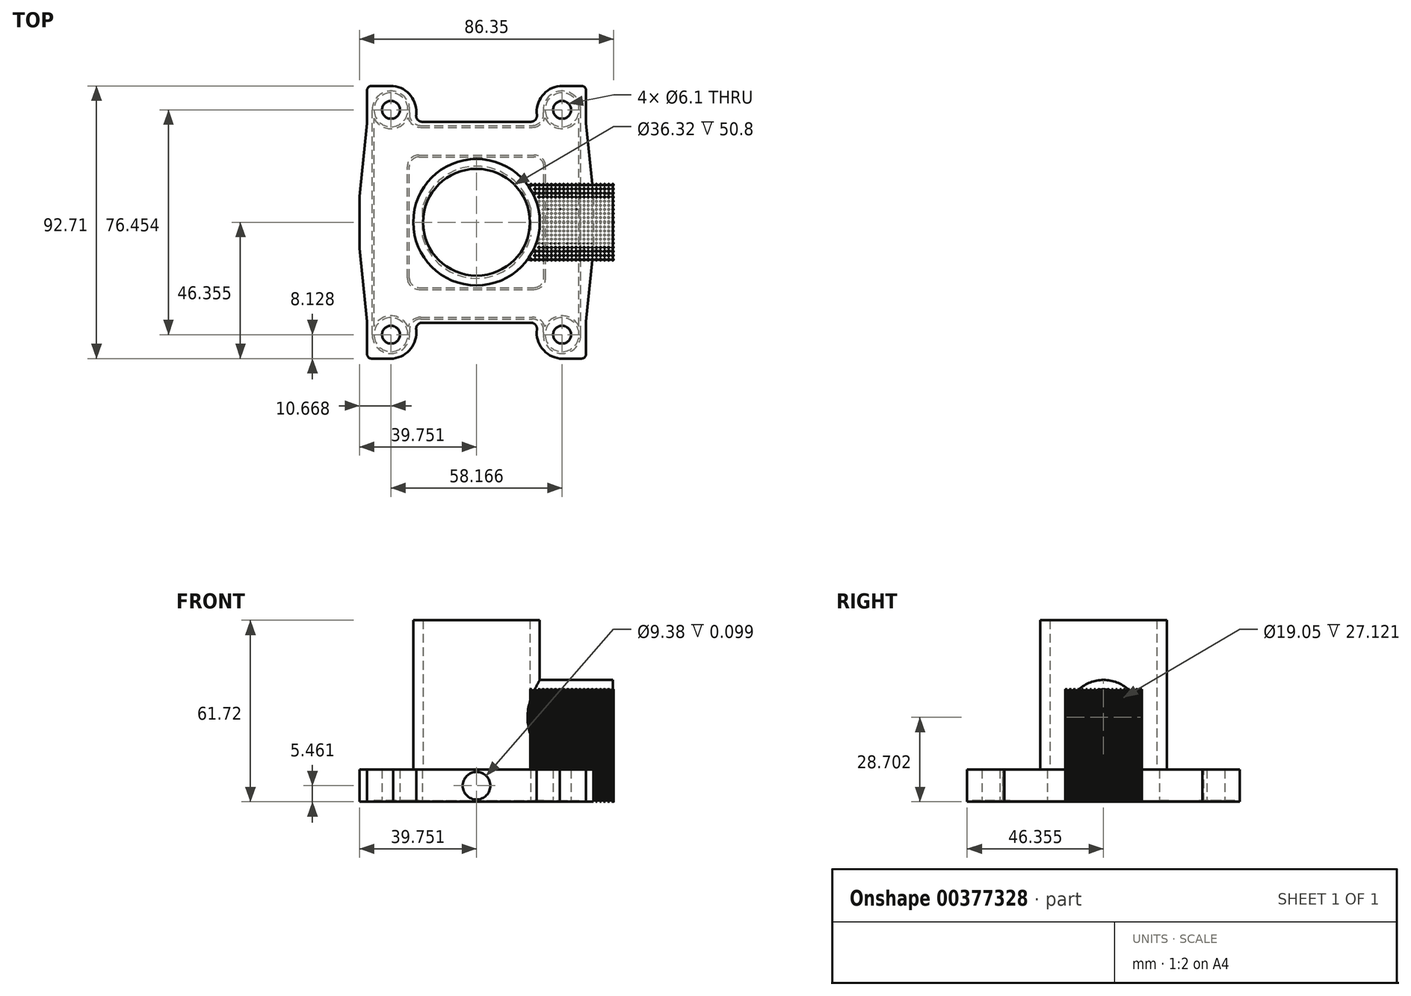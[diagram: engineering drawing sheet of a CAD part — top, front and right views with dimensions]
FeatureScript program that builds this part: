
annotation { "Feature Type Name" : "Feature", "Feature Type Description" : "" }
export const myFeature = defineFeature(function(context is Context, id is Id, definition is map)
    precondition{}
    {
        {
            var Q0;
            Q0=qCreatedBy(makeId("Top.planeOp"),FACE);
            var sketch = newSketch(context, id + "F0", { "sketchPlane" : qUnion([Q0])});
            skLineSegment(sketch, "E0.bottom", {"start": v(0, 0) * mm, "end": v(74.42, 0) * mm});
            skLineSegment(sketch, "E0.top", {"start": v(0, 92.7) * mm, "end": v(74.42, 92.7) * mm});
            skLineSegment(sketch, "E0.left", {"start": v(0, 0) * mm, "end": v(0, 12.7) * mm});
            skLineSegment(sketch, "E0.right", {"start": v(74.42, 0) * mm, "end": v(74.42, 92.7) * mm});
            skCircle(sketch, "E1", {"center": v(8.13, 84.58) * mm, "radius": 3.05 * mm});
            skCircle(sketch, "E2", {"center": v(66.3, 84.58) * mm, "radius": 3.05 * mm});
            skCircle(sketch, "E3", {"center": v(8.13, 8.13) * mm, "radius": 3.05 * mm});
            skCircle(sketch, "E4", {"center": v(66.3, 8.13) * mm, "radius": 3.05 * mm});
            skArc(sketch, "E5", {"start": v(18.8, 41.48) * mm, "mid": v(37.21, 27.3) * mm, "end": v(55.63, 41.48) * mm});
            skLineSegment(sketch, "E6", {"start": v(18.8, 51.23) * mm, "end": v(18.8, 41.48) * mm});
            skLineSegment(sketch, "E7", {"start": v(55.63, 51.23) * mm, "end": v(55.63, 41.48) * mm});
            skArc(sketch, "E8.trimOffspring", {"start": v(55.63, 51.23) * mm, "mid": v(37.21, 65.4) * mm, "end": v(18.8, 51.23) * mm});
            skLineSegment(sketch, "E9", {"start": v(11.94, 80.52) * mm, "end": v(57.51, 80.52) * mm});
            skLineSegment(sketch, "E10", {"start": v(11.94, 12.2) * mm, "end": v(57.51, 12.2) * mm});
            skLineSegment(sketch, "E11", {"start": v(0, 80) * mm, "end": v(-2.54, 55.25) * mm});
            skLineSegment(sketch, "E12", {"start": v(-2.54, 55.25) * mm, "end": v(-2.54, 37.47) * mm});
            skLineSegment(sketch, "E13", {"start": v(-2.54, 37.47) * mm, "end": v(0, 12.7) * mm});
            skLineSegment(sketch, "E14", {"start": v(37.21, 55.66) * mm, "end": v(37.21, 36.27) * mm});
            skLineSegment(sketch, "E15.MirrorCS", {"start": v(76.96, 55.25) * mm, "end": v(76.96, 37.47) * mm});
            skLineSegment(sketch, "E16.MirrorCS", {"start": v(74.42, 80) * mm, "end": v(76.96, 55.25) * mm});
            skLineSegment(sketch, "E17.MirrorCS", {"start": v(76.96, 37.47) * mm, "end": v(74.42, 12.7) * mm});
            skLineSegment(sketch, "E18.trimOffspring", {"start": v(0, 80) * mm, "end": v(0, 92.7) * mm});
            skSolve(sketch);
        }
        {
            var Q0;
            Q0=makeQuery(id+"F0.imprint","IMPRINT",FACE,{"disambiguationData":[TD([[makeQuery(id+"F0.imprint","IMPRINT",EDGE,{"derivedFrom":sQuery(id+"F0.wireOp",EDGE,"E0.bottom")}),1.0]])]});
            var Q1;
            Q1=makeQuery(id+"F0.imprint","IMPRINT",FACE,{"disambiguationData":[TD([[makeQuery(id+"F0.imprint","IMPRINT",EDGE,{"derivedFrom":sQuery(id+"F0.wireOp",EDGE,"E15.MirrorCS")}),-1.0]])]});
            extrude(context, id + "F1", {"entities" : qUnion([Q0, Q1]), "depth" : 10.92 * mm});
        }
        {
            var Q0;
            Q0=makeQuery(id+"F1.opExtrude","CAP_FACE",FACE,{"disambiguationData":[OSD([sQuery(id+"F0.wireOp",EDGE,"E0.bottom"),sQuery(id+"F0.wireOp",EDGE,"E0.top"),sQuery(id+"F0.wireOp",EDGE,"E0.left"),sQuery(id+"F0.wireOp",EDGE,"E0.right"),sQuery(id+"F0.wireOp",EDGE,"E1"),sQuery(id+"F0.wireOp",EDGE,"E2"),sQuery(id+"F0.wireOp",EDGE,"E3"),sQuery(id+"F0.wireOp",EDGE,"E4"),sQuery(id+"F0.wireOp",EDGE,"E5"),sQuery(id+"F0.wireOp",EDGE,"E6"),sQuery(id+"F0.wireOp",EDGE,"E7"),sQuery(id+"F0.wireOp",EDGE,"E8.trimOffspring"),sQuery(id+"F0.wireOp",EDGE,"E11"),sQuery(id+"F0.wireOp",EDGE,"E12"),sQuery(id+"F0.wireOp",EDGE,"E13"),sQuery(id+"F0.wireOp",EDGE,"E15.MirrorCS"),sQuery(id+"F0.wireOp",EDGE,"E16.MirrorCS"),sQuery(id+"F0.wireOp",EDGE,"E17.MirrorCS"),sQuery(id+"F0.wireOp",EDGE,"E18.trimOffspring")])],"isStart":false});
            var sketch = newSketch(context, id + "F2", { "sketchPlane" : qUnion([Q0])});
            skLineSegment(sketch, "E19", {"start": v(16.13, 80.52) * mm, "end": v(58.3, 80.52) * mm});
            skLineSegment(sketch, "E20", {"start": v(16.13, 12.2) * mm, "end": v(58.3, 12.2) * mm});
            skArc(sketch, "E21", {"start": v(16.13, 80.52) * mm, "mid": v(14.87, 89.31) * mm, "end": v(6.67, 92.7) * mm});
            skArc(sketch, "E22", {"start": v(65.5, 92.7) * mm, "mid": v(58.91, 88.38) * mm, "end": v(58.3, 80.52) * mm});
            skArc(sketch, "E23", {"start": v(8.92, 0) * mm, "mid": v(15.5, 4.33) * mm, "end": v(16.13, 12.2) * mm});
            skArc(sketch, "E24", {"start": v(58.3, 12.2) * mm, "mid": v(58.91, 4.33) * mm, "end": v(65.5, 0) * mm});
            skLineSegment(sketch, "E25", {"start": v(6.67, 92.7) * mm, "end": v(65.5, 92.7) * mm});
            skLineSegment(sketch, "E26", {"start": v(8.92, 0) * mm, "end": v(65.5, 0) * mm});
            skSolve(sketch);
        }
        {
            var Q0;
            {var subQ0=sQuery(id+"F2.wireOp",EDGE,"E19");Q0=makeQuery(id+"F2.imprint","IMPRINT",FACE,{"disambiguationData":[TD([[makeQuery(id+"F2.imprint","IMPRINT",EDGE,{"derivedFrom":subQ0}),1.0]])]});}
            var Q1;
            Q1=makeQuery(id+"F2.imprint","IMPRINT",FACE,{"disambiguationData":[TD([[makeQuery(id+"F2.imprint","IMPRINT",EDGE,{"derivedFrom":sQuery(id+"F2.wireOp",EDGE,"E20")}),-1.0]])]});
            extrude(context, id + "F3", {"entities" : qUnion([Q0, Q1]), "operationType" : NewBodyOperationType.REMOVE, "endBound" : BoundingType.THROUGH_ALL, "oppositeDirection" : true, "depth" : 25 * mm});
        }
        {
            var Q0;
            Q0=makeQuery(id+"F3.boolean.opBoolean","COPY",EDGE,{"derivedFrom":makeQuery(id+"F3.opExtrude","SWEPT_EDGE",EDGE,{"disambiguationData":[OSD([sQuery(id+"F2.wireOp",EDGE,"E19"),sQuery(id+"F2.wireOp",EDGE,"E21")])]})});
            var Q1;
            Q1=makeQuery(id+"F3.boolean.opBoolean","COPY",EDGE,{"derivedFrom":makeQuery(id+"F3.opExtrude","SWEPT_EDGE",EDGE,{"disambiguationData":[OSD([sQuery(id+"F2.wireOp",EDGE,"E19"),sQuery(id+"F2.wireOp",EDGE,"E22")])]})});
            var Q2;
            Q2=makeQuery(id+"F3.boolean.opBoolean","COPY",EDGE,{"derivedFrom":makeQuery(id+"F3.opExtrude","SWEPT_EDGE",EDGE,{"disambiguationData":[OSD([sQuery(id+"F2.wireOp",EDGE,"E20"),sQuery(id+"F2.wireOp",EDGE,"E24")])]})});
            var Q3;
            Q3=makeQuery(id+"F3.boolean.opBoolean","COPY",EDGE,{"derivedFrom":makeQuery(id+"F3.opExtrude","SWEPT_EDGE",EDGE,{"disambiguationData":[OSD([sQuery(id+"F2.wireOp",EDGE,"E20"),sQuery(id+"F2.wireOp",EDGE,"E23")])]})});
            fillet(context, id + "F4", {"entities" : qUnion([Q0, Q1, Q2, Q3]), "radius" : 2.03 * mm, "tangentPropagation" : true, "allowEdgeOverflow" : false});
        }
        {
            var Q0;
            Q0=makeQuery(id+"F1.opExtrude","SWEPT_EDGE",EDGE,{"disambiguationData":[OSD([sQuery(id+"F0.wireOp",EDGE,"E0.top"),sQuery(id+"F0.wireOp",EDGE,"E18.trimOffspring")])]});
            var Q1;
            Q1=makeQuery(id+"F1.opExtrude","SWEPT_EDGE",EDGE,{"disambiguationData":[OSD([sQuery(id+"F0.wireOp",EDGE,"E0.bottom"),sQuery(id+"F0.wireOp",EDGE,"E0.left")])]});
            var Q2;
            Q2=makeQuery(id+"F1.opExtrude","SWEPT_EDGE",EDGE,{"disambiguationData":[OSD([sQuery(id+"F0.wireOp",EDGE,"E0.bottom"),sQuery(id+"F0.wireOp",EDGE,"E0.right")])]});
            var Q3;
            Q3=makeQuery(id+"F1.opExtrude","SWEPT_EDGE",EDGE,{"disambiguationData":[OSD([sQuery(id+"F0.wireOp",EDGE,"E0.top"),sQuery(id+"F0.wireOp",EDGE,"E0.right")])]});
            fillet(context, id + "F5", {"entities" : qUnion([Q0, Q1, Q2, Q3]), "radius" : 1.52 * mm, "tangentPropagation" : true, "allowEdgeOverflow" : false});
        }
        {
            var Q0;
            Q0=makeQuery(id+"F1.opExtrude","CAP_FACE",FACE,{"disambiguationData":[OSD([sQuery(id+"F0.wireOp",EDGE,"E0.bottom"),sQuery(id+"F0.wireOp",EDGE,"E0.top"),sQuery(id+"F0.wireOp",EDGE,"E0.left"),sQuery(id+"F0.wireOp",EDGE,"E0.right"),sQuery(id+"F0.wireOp",EDGE,"E1"),sQuery(id+"F0.wireOp",EDGE,"E2"),sQuery(id+"F0.wireOp",EDGE,"E3"),sQuery(id+"F0.wireOp",EDGE,"E4"),sQuery(id+"F0.wireOp",EDGE,"E5"),sQuery(id+"F0.wireOp",EDGE,"E6"),sQuery(id+"F0.wireOp",EDGE,"E7"),sQuery(id+"F0.wireOp",EDGE,"E8.trimOffspring"),sQuery(id+"F0.wireOp",EDGE,"E11"),sQuery(id+"F0.wireOp",EDGE,"E12"),sQuery(id+"F0.wireOp",EDGE,"E13"),sQuery(id+"F0.wireOp",EDGE,"E15.MirrorCS"),sQuery(id+"F0.wireOp",EDGE,"E16.MirrorCS"),sQuery(id+"F0.wireOp",EDGE,"E17.MirrorCS"),sQuery(id+"F0.wireOp",EDGE,"E18.trimOffspring")])],"isStart":true});
            var sketch = newSketch(context, id + "F6", { "sketchPlane" : qUnion([Q0])});
            skLineSegment(sketch, "E27", {"start": v(1.73, -8.13) * mm, "end": v(1.73, -84.58) * mm});
            skLineSegment(sketch, "E28", {"start": v(2.36, -10.9) * mm, "end": v(2.36, -81.8) * mm});
            skArc(sketch, "E29", {"start": v(2.36, -10.9) * mm, "mid": v(8.2, -14.53) * mm, "end": v(13.96, -10.78) * mm});
            skCircle(sketch, "E30", {"center": v(8.13, -8.13) * mm, "radius": 5.77 * mm});
            skLineSegment(sketch, "E31", {"start": v(37.21, -46.35) * mm, "end": v(50.56, -46.35) * mm});
            skPoint(sketch, "E31.endSnap0", {"position": v(55.63, -46.35) * mm});
            skLineSegment(sketch, "E32", {"start": v(37.21, -46.35) * mm, "end": v(37.21, -35.15) * mm});
            skArc(sketch, "E33.MirrorC", {"start": v(72.06, -10.9) * mm, "mid": v(66.22, -14.53) * mm, "end": v(60.47, -10.78) * mm});
            skCircle(sketch, "E34.MirrorC", {"center": v(66.3, -8.13) * mm, "radius": 5.77 * mm});
            skArc(sketch, "E35.MirrorC", {"start": v(2.36, -81.8) * mm, "mid": v(8.2, -78.18) * mm, "end": v(13.96, -81.93) * mm});
            skCircle(sketch, "E36.MirrorC", {"center": v(8.13, -84.58) * mm, "radius": 5.77 * mm});
            skArc(sketch, "E37.MirrorC", {"start": v(72.06, -81.8) * mm, "mid": v(66.22, -78.18) * mm, "end": v(60.47, -81.93) * mm});
            skCircle(sketch, "E38.MirrorC", {"center": v(66.3, -84.58) * mm, "radius": 5.77 * mm});
            skLineSegment(sketch, "E39.MirrorCS", {"start": v(72.7, -8.13) * mm, "end": v(72.7, -84.58) * mm});
            skLineSegment(sketch, "E40.MirrorCS", {"start": v(72.06, -10.9) * mm, "end": v(72.06, -81.8) * mm});
            skLineSegment(sketch, "E41", {"start": v(18.32, -13.46) * mm, "end": v(56.1, -13.46) * mm});
            skLineSegment(sketch, "E42", {"start": v(18.32, -14.1) * mm, "end": v(56.1, -14.1) * mm});
            skArc(sketch, "E43", {"start": v(56.1, -14.1) * mm, "mid": v(58.85, -13.17) * mm, "end": v(60.47, -10.78) * mm});
            skArc(sketch, "E44", {"start": v(13.96, -10.78) * mm, "mid": v(15.58, -13.17) * mm, "end": v(18.32, -14.1) * mm});
            skArc(sketch, "E45", {"start": v(14.47, -9.03) * mm, "mid": v(15.38, -12.12) * mm, "end": v(18.32, -13.46) * mm});
            skArc(sketch, "E46", {"start": v(56.1, -13.46) * mm, "mid": v(59.04, -12.12) * mm, "end": v(59.96, -9.03) * mm});
            skArc(sketch, "E47.trimOffspring", {"start": v(14.47, -9.03) * mm, "mid": v(8.58, -1.74) * mm, "end": v(1.73, -8.13) * mm});
            skArc(sketch, "E48.trimOffspring", {"start": v(59.96, -9.03) * mm, "mid": v(65.84, -1.74) * mm, "end": v(72.7, -8.13) * mm});
            skArc(sketch, "E49.MirrorCS", {"start": v(13.96, -81.93) * mm, "mid": v(15.58, -79.54) * mm, "end": v(18.32, -78.61) * mm});
            skArc(sketch, "E50.MirrorCS", {"start": v(14.47, -83.68) * mm, "mid": v(15.38, -80.59) * mm, "end": v(18.32, -79.25) * mm});
            skLineSegment(sketch, "E51.MirrorCS", {"start": v(18.32, -79.25) * mm, "end": v(56.1, -79.25) * mm});
            skLineSegment(sketch, "E52.MirrorCS", {"start": v(18.32, -78.61) * mm, "end": v(56.1, -78.61) * mm});
            skArc(sketch, "E53.MirrorCS", {"start": v(56.1, -78.61) * mm, "mid": v(58.85, -79.54) * mm, "end": v(60.47, -81.93) * mm});
            skArc(sketch, "E54.MirrorCS", {"start": v(56.1, -79.25) * mm, "mid": v(59.04, -80.59) * mm, "end": v(59.96, -83.68) * mm});
            skArc(sketch, "E55.trimOffspring", {"start": v(14.47, -83.68) * mm, "mid": v(8.58, -90.97) * mm, "end": v(1.73, -84.58) * mm});
            skArc(sketch, "E56.trimOffspring", {"start": v(59.96, -83.68) * mm, "mid": v(65.84, -90.97) * mm, "end": v(72.7, -84.58) * mm});
            skLineSegment(sketch, "E57", {"start": v(13.72, -27.43) * mm, "end": v(13.72, -65.28) * mm});
            skLineSegment(sketch, "E58", {"start": v(14.35, -27.43) * mm, "end": v(14.35, -65.28) * mm});
            skLineSegment(sketch, "E59", {"start": v(17.65, -23.5) * mm, "end": v(56.77, -23.5) * mm});
            skLineSegment(sketch, "E60", {"start": v(17.65, -24.13) * mm, "end": v(56.77, -24.13) * mm});
            skArc(sketch, "E61", {"start": v(17.65, -23.5) * mm, "mid": v(14.87, -24.65) * mm, "end": v(13.72, -27.43) * mm});
            skArc(sketch, "E62", {"start": v(17.65, -24.13) * mm, "mid": v(15.32, -25.1) * mm, "end": v(14.35, -27.43) * mm});
            skArc(sketch, "E63.MirrorCS", {"start": v(56.77, -24.13) * mm, "mid": v(59.1, -25.1) * mm, "end": v(60.07, -27.43) * mm});
            skArc(sketch, "E64.MirrorCS", {"start": v(56.77, -23.5) * mm, "mid": v(59.55, -24.65) * mm, "end": v(60.7, -27.43) * mm});
            skLineSegment(sketch, "E65.MirrorCS", {"start": v(60.7, -27.43) * mm, "end": v(60.7, -65.28) * mm});
            skLineSegment(sketch, "E66.MirrorCS", {"start": v(60.07, -27.43) * mm, "end": v(60.07, -65.28) * mm});
            skLineSegment(sketch, "E67.MirrorCS", {"start": v(17.65, -69.22) * mm, "end": v(56.77, -69.22) * mm});
            skLineSegment(sketch, "E68.MirrorCS", {"start": v(17.65, -68.58) * mm, "end": v(56.77, -68.58) * mm});
            skArc(sketch, "E69.MirrorCS", {"start": v(56.77, -68.58) * mm, "mid": v(59.1, -67.61) * mm, "end": v(60.07, -65.28) * mm});
            skArc(sketch, "E70.MirrorCS", {"start": v(56.77, -69.22) * mm, "mid": v(59.55, -68.06) * mm, "end": v(60.7, -65.28) * mm});
            skArc(sketch, "E71.MirrorCS", {"start": v(17.65, -68.58) * mm, "mid": v(15.32, -67.61) * mm, "end": v(14.35, -65.28) * mm});
            skArc(sketch, "E72.MirrorCS", {"start": v(17.65, -69.22) * mm, "mid": v(14.87, -68.06) * mm, "end": v(13.72, -65.28) * mm});
            skSolve(sketch);
        }
        {
            var Q0;
            Q0=makeQuery(id+"F6.imprint","IMPRINT",FACE,{"disambiguationData":[TD([[makeQuery(id+"F6.imprint","IMPRINT",EDGE,{"derivedFrom":sQuery(id+"F6.wireOp",EDGE,"E27")}),1.0]])]});
            var Q1;
            Q1=makeQuery(id+"F6.imprint","IMPRINT",FACE,{"disambiguationData":[TD([[makeQuery(id+"F6.imprint","IMPRINT",EDGE,{"derivedFrom":sQuery(id+"F6.wireOp",EDGE,"E57")}),1.0]])]});
            extrude(context, id + "F7", {"entities" : qUnion([Q0, Q1]), "operationType" : NewBodyOperationType.REMOVE, "oppositeDirection" : true, "depth" : 0.38 * mm});
        }
        {
            var Q0;
            Q0=makeQuery(id+"F1.opExtrude","CAP_FACE",FACE,{"disambiguationData":[OSD([sQuery(id+"F0.wireOp",EDGE,"E0.bottom"),sQuery(id+"F0.wireOp",EDGE,"E0.top"),sQuery(id+"F0.wireOp",EDGE,"E0.left"),sQuery(id+"F0.wireOp",EDGE,"E0.right"),sQuery(id+"F0.wireOp",EDGE,"E1"),sQuery(id+"F0.wireOp",EDGE,"E2"),sQuery(id+"F0.wireOp",EDGE,"E3"),sQuery(id+"F0.wireOp",EDGE,"E4"),sQuery(id+"F0.wireOp",EDGE,"E5"),sQuery(id+"F0.wireOp",EDGE,"E6"),sQuery(id+"F0.wireOp",EDGE,"E7"),sQuery(id+"F0.wireOp",EDGE,"E8.trimOffspring"),sQuery(id+"F0.wireOp",EDGE,"E11"),sQuery(id+"F0.wireOp",EDGE,"E12"),sQuery(id+"F0.wireOp",EDGE,"E13"),sQuery(id+"F0.wireOp",EDGE,"E15.MirrorCS"),sQuery(id+"F0.wireOp",EDGE,"E16.MirrorCS"),sQuery(id+"F0.wireOp",EDGE,"E17.MirrorCS"),sQuery(id+"F0.wireOp",EDGE,"E18.trimOffspring")])],"isStart":false});
            var sketch = newSketch(context, id + "F8", { "sketchPlane" : qUnion([Q0])});
            skCircle(sketch, "E73", {"center": v(37.21, 46.35) * mm, "radius": 18.16 * mm});
            skCircle(sketch, "E74", {"center": v(37.21, 46.35) * mm, "radius": 21.5 * mm});
            skSolve(sketch);
        }
        {
            var Q0;
            Q0 = qSketchRegion(id + "F8", true);
            extrude(context, id + "F9", {"entities" : qUnion([Q0]), "operationType" : NewBodyOperationType.ADD, "depth" : 50.8 * mm});
        }
        {
            var Q0;
            Q0=qCreatedBy(makeId("Right.planeOp"),FACE);
            cPlane(context, id + "F10", {"entities" : qUnion([Q0]), "cplaneType" : CPlaneType.OFFSET, "offset" : 37.21 * mm, "width" : 150 * mm, "height" : 150 * mm});
        }
        {
            var Q0;
            Q0=qCreatedBy(id+"F10.planeOp",FACE);
            var sketch = newSketch(context, id + "F11", { "sketchPlane" : qUnion([Q0])});
            skCircle(sketch, "E75", {"center": v(46.35, 28.7) * mm, "radius": 9.53 * mm});
            skCircle(sketch, "E76", {"center": v(46.35, 28.7) * mm, "radius": 12.7 * mm});
            skSolve(sketch);
        }
        {
            var Q0;
            Q0 = qSketchRegion(id + "F11", true);
            var Q1;
            Q1=makeQuery(id+"F9.opExtrude","SWEPT_FACE",FACE,{"disambiguationData":[OSD([sQuery(id+"F8.wireOp",EDGE,"E74")])]});
            extrude(context, id + "F12", {"entities" : qUnion([Q0]), "operationType" : NewBodyOperationType.ADD, "endBoundEntityFace" : qUnion([Q1]), "depth" : (43 * mm / 2) + 24.9 * mm});
        }
        {
            var Q0;
            Q0=makeQuery(id+"F9.opExtrude","CAP_FACE",FACE,{"disambiguationData":[OSD([sQuery(id+"F8.wireOp",EDGE,"E73"),sQuery(id+"F8.wireOp",EDGE,"E74")])],"isStart":false});
            var sketch = newSketch(context, id + "F13", { "sketchPlane" : qUnion([Q0])});
            skCircle(sketch, "E77", {"center": v(37.21, 46.35) * mm, "radius": 18.16 * mm});
            skSolve(sketch);
        }
        {
            var Q0;
            Q0 = qSketchRegion(id + "F13", true);
            extrude(context, id + "F14", {"entities" : qUnion([Q0]), "operationType" : NewBodyOperationType.REMOVE, "endBound" : BoundingType.THROUGH_ALL, "oppositeDirection" : true, "depth" : 25 * mm});
        }
        {
            var Q0;
            Q0=qCreatedBy(makeId("Top.planeOp"),FACE);
            cPlane(context, id + "F15", {"entities" : qUnion([Q0]), "cplaneType" : CPlaneType.OFFSET, "offset" : 10.92 * mm, "width" : 150 * mm, "height" : 150 * mm});
        }
        {
            var Q0;
            Q0=qCreatedBy(id+"F15.planeOp",FACE);
            var sketch = newSketch(context, id + "F16", { "sketchPlane" : qUnion([Q0])});
            skCircle(sketch, "E78", {"center": v(55.73, 59.05) * mm, "radius": 0.3 * mm});
            skCircle(sketch, "E79.1.0.0", {"center": v(57.12, 59.05) * mm, "radius": 0.3 * mm});
            skCircle(sketch, "E79.2.0.0", {"center": v(58.5, 59.05) * mm, "radius": 0.3 * mm});
            skCircle(sketch, "E79.3.0.0", {"center": v(59.9, 59.05) * mm, "radius": 0.3 * mm});
            skCircle(sketch, "E79.4.0.0", {"center": v(61.29, 59.05) * mm, "radius": 0.3 * mm});
            skCircle(sketch, "E79.5.0.0", {"center": v(62.67, 59.05) * mm, "radius": 0.3 * mm});
            skCircle(sketch, "E79.6.0.0", {"center": v(64.06, 59.05) * mm, "radius": 0.3 * mm});
            skCircle(sketch, "E79.7.0.0", {"center": v(65.45, 59.05) * mm, "radius": 0.3 * mm});
            skCircle(sketch, "E79.8.0.0", {"center": v(66.84, 59.05) * mm, "radius": 0.3 * mm});
            skCircle(sketch, "E79.9.0.0", {"center": v(68.23, 59.05) * mm, "radius": 0.3 * mm});
            skCircle(sketch, "E79.10.0.0", {"center": v(69.62, 59.05) * mm, "radius": 0.3 * mm});
            skCircle(sketch, "E79.11.0.0", {"center": v(71, 59.05) * mm, "radius": 0.3 * mm});
            skCircle(sketch, "E79.12.0.0", {"center": v(72.4, 59.05) * mm, "radius": 0.3 * mm});
            skCircle(sketch, "E79.13.0.0", {"center": v(73.79, 59.05) * mm, "radius": 0.3 * mm});
            skCircle(sketch, "E79.14.0.0", {"center": v(75.18, 59.05) * mm, "radius": 0.3 * mm});
            skCircle(sketch, "E79.15.0.0", {"center": v(76.56, 59.05) * mm, "radius": 0.3 * mm});
            skLineSegment(sketch, "E79.direction1", {"start": v(55.73, 59.05) * mm, "end": v(57.12, 59.05) * mm, "construction": true});
            skCircle(sketch, "E80", {"center": v(55.73, 33.66) * mm, "radius": 0.3 * mm});
            skCircle(sketch, "E81.1.0.0", {"center": v(57.12, 33.66) * mm, "radius": 0.3 * mm});
            skCircle(sketch, "E81.2.0.0", {"center": v(58.5, 33.66) * mm, "radius": 0.3 * mm});
            skCircle(sketch, "E81.3.0.0", {"center": v(59.9, 33.66) * mm, "radius": 0.3 * mm});
            skCircle(sketch, "E81.4.0.0", {"center": v(61.29, 33.66) * mm, "radius": 0.3 * mm});
            skCircle(sketch, "E81.5.0.0", {"center": v(62.67, 33.66) * mm, "radius": 0.3 * mm});
            skCircle(sketch, "E81.6.0.0", {"center": v(64.06, 33.66) * mm, "radius": 0.3 * mm});
            skCircle(sketch, "E81.7.0.0", {"center": v(65.45, 33.66) * mm, "radius": 0.3 * mm});
            skCircle(sketch, "E81.8.0.0", {"center": v(66.84, 33.66) * mm, "radius": 0.3 * mm});
            skCircle(sketch, "E81.9.0.0", {"center": v(68.23, 33.66) * mm, "radius": 0.3 * mm});
            skCircle(sketch, "E81.10.0.0", {"center": v(69.62, 33.66) * mm, "radius": 0.3 * mm});
            skCircle(sketch, "E81.11.0.0", {"center": v(71, 33.66) * mm, "radius": 0.3 * mm});
            skCircle(sketch, "E81.12.0.0", {"center": v(72.4, 33.66) * mm, "radius": 0.3 * mm});
            skCircle(sketch, "E81.13.0.0", {"center": v(73.79, 33.66) * mm, "radius": 0.3 * mm});
            skCircle(sketch, "E81.14.0.0", {"center": v(75.18, 33.66) * mm, "radius": 0.3 * mm});
            skCircle(sketch, "E81.15.0.0", {"center": v(76.56, 33.66) * mm, "radius": 0.3 * mm});
            skLineSegment(sketch, "E81.direction1", {"start": v(55.73, 33.66) * mm, "end": v(57.12, 33.66) * mm, "construction": true});
            skCircle(sketch, "E82.1.0.0", {"center": v(57.12, 57.66) * mm, "radius": 0.3 * mm});
            skCircle(sketch, "E82.2.0.0", {"center": v(57.12, 56.27) * mm, "radius": 0.3 * mm});
            skLineSegment(sketch, "E82.direction1", {"start": v(57.12, 59.05) * mm, "end": v(57.12, 57.66) * mm, "construction": true});
            skCircle(sketch, "E83.1.0.0", {"center": v(57.12, 35.04) * mm, "radius": 0.3 * mm});
            skCircle(sketch, "E83.2.0.0", {"center": v(57.12, 36.43) * mm, "radius": 0.3 * mm});
            skLineSegment(sketch, "E83.direction1", {"start": v(57.12, 33.66) * mm, "end": v(57.12, 35.04) * mm, "construction": true});
            skCircle(sketch, "E84.1.0.0", {"center": v(58.5, 57.66) * mm, "radius": 0.3 * mm});
            skCircle(sketch, "E84.2.0.0", {"center": v(58.5, 56.27) * mm, "radius": 0.3 * mm});
            skCircle(sketch, "E84.3.0.0", {"center": v(58.5, 54.88) * mm, "radius": 0.3 * mm});
            skCircle(sketch, "E84.4.0.0", {"center": v(58.5, 53.5) * mm, "radius": 0.3 * mm});
            skCircle(sketch, "E84.5.0.0", {"center": v(58.5, 52.1) * mm, "radius": 0.3 * mm});
            skLineSegment(sketch, "E84.direction1", {"start": v(58.5, 59.05) * mm, "end": v(58.5, 57.66) * mm, "construction": true});
            skCircle(sketch, "E85.1.0.0", {"center": v(59.9, 57.66) * mm, "radius": 0.3 * mm});
            skCircle(sketch, "E85.2.0.0", {"center": v(59.9, 56.27) * mm, "radius": 0.3 * mm});
            skCircle(sketch, "E85.3.0.0", {"center": v(59.9, 54.88) * mm, "radius": 0.3 * mm});
            skCircle(sketch, "E85.4.0.0", {"center": v(59.9, 53.5) * mm, "radius": 0.3 * mm});
            skCircle(sketch, "E85.5.0.0", {"center": v(59.9, 52.1) * mm, "radius": 0.3 * mm});
            skCircle(sketch, "E85.6.0.0", {"center": v(59.9, 50.72) * mm, "radius": 0.3 * mm});
            skCircle(sketch, "E85.7.0.0", {"center": v(59.9, 49.33) * mm, "radius": 0.3 * mm});
            skCircle(sketch, "E85.8.0.0", {"center": v(59.9, 47.94) * mm, "radius": 0.3 * mm});
            skLineSegment(sketch, "E85.direction1", {"start": v(59.9, 59.05) * mm, "end": v(59.9, 57.66) * mm, "construction": true});
            skCircle(sketch, "E86.1.0.0", {"center": v(58.5, 35.04) * mm, "radius": 0.3 * mm});
            skCircle(sketch, "E86.2.0.0", {"center": v(58.5, 36.43) * mm, "radius": 0.3 * mm});
            skCircle(sketch, "E86.3.0.0", {"center": v(58.5, 37.82) * mm, "radius": 0.3 * mm});
            skCircle(sketch, "E86.4.0.0", {"center": v(58.5, 39.21) * mm, "radius": 0.3 * mm});
            skCircle(sketch, "E86.5.0.0", {"center": v(58.5, 40.6) * mm, "radius": 0.3 * mm});
            skLineSegment(sketch, "E86.direction1", {"start": v(58.5, 33.66) * mm, "end": v(58.5, 35.04) * mm, "construction": true});
            skCircle(sketch, "E87.1.0.0", {"center": v(59.9, 35.04) * mm, "radius": 0.3 * mm});
            skCircle(sketch, "E87.2.0.0", {"center": v(59.9, 36.43) * mm, "radius": 0.3 * mm});
            skCircle(sketch, "E87.3.0.0", {"center": v(59.9, 37.82) * mm, "radius": 0.3 * mm});
            skCircle(sketch, "E87.4.0.0", {"center": v(59.9, 39.21) * mm, "radius": 0.3 * mm});
            skCircle(sketch, "E87.5.0.0", {"center": v(59.9, 40.6) * mm, "radius": 0.3 * mm});
            skCircle(sketch, "E87.6.0.0", {"center": v(59.9, 42) * mm, "radius": 0.3 * mm});
            skCircle(sketch, "E87.7.0.0", {"center": v(59.9, 43.38) * mm, "radius": 0.3 * mm});
            skCircle(sketch, "E87.8.0.0", {"center": v(59.9, 44.77) * mm, "radius": 0.3 * mm});
            skCircle(sketch, "E87.9.0.0", {"center": v(59.9, 46.16) * mm, "radius": 0.3 * mm});
            skLineSegment(sketch, "E87.direction1", {"start": v(59.9, 33.66) * mm, "end": v(59.9, 35.04) * mm, "construction": true});
            skCircle(sketch, "E88.1.0.0", {"center": v(61.29, 57.66) * mm, "radius": 0.3 * mm});
            skCircle(sketch, "E88.2.0.0", {"center": v(61.29, 56.27) * mm, "radius": 0.3 * mm});
            skCircle(sketch, "E88.3.0.0", {"center": v(61.29, 54.88) * mm, "radius": 0.3 * mm});
            skCircle(sketch, "E88.4.0.0", {"center": v(61.29, 53.5) * mm, "radius": 0.3 * mm});
            skCircle(sketch, "E88.5.0.0", {"center": v(61.29, 52.1) * mm, "radius": 0.3 * mm});
            skCircle(sketch, "E88.6.0.0", {"center": v(61.29, 50.72) * mm, "radius": 0.3 * mm});
            skCircle(sketch, "E88.7.0.0", {"center": v(61.29, 49.33) * mm, "radius": 0.3 * mm});
            skCircle(sketch, "E88.8.0.0", {"center": v(61.29, 47.94) * mm, "radius": 0.3 * mm});
            skCircle(sketch, "E88.9.0.0", {"center": v(61.29, 46.55) * mm, "radius": 0.3 * mm});
            skLineSegment(sketch, "E88.direction1", {"start": v(61.29, 59.05) * mm, "end": v(61.29, 57.66) * mm, "construction": true});
            skCircle(sketch, "E89.1.0.0", {"center": v(61.29, 35.04) * mm, "radius": 0.3 * mm});
            skCircle(sketch, "E89.2.0.0", {"center": v(61.29, 36.43) * mm, "radius": 0.3 * mm});
            skCircle(sketch, "E89.3.0.0", {"center": v(61.29, 37.82) * mm, "radius": 0.3 * mm});
            skCircle(sketch, "E89.4.0.0", {"center": v(61.29, 39.21) * mm, "radius": 0.3 * mm});
            skCircle(sketch, "E89.5.0.0", {"center": v(61.29, 40.6) * mm, "radius": 0.3 * mm});
            skCircle(sketch, "E89.6.0.0", {"center": v(61.29, 42) * mm, "radius": 0.3 * mm});
            skCircle(sketch, "E89.7.0.0", {"center": v(61.29, 43.38) * mm, "radius": 0.3 * mm});
            skCircle(sketch, "E89.8.0.0", {"center": v(61.29, 44.77) * mm, "radius": 0.3 * mm});
            skLineSegment(sketch, "E89.direction1", {"start": v(61.29, 33.66) * mm, "end": v(61.29, 35.04) * mm, "construction": true});
            skCircle(sketch, "E90.1.0.0", {"center": v(62.67, 35.04) * mm, "radius": 0.3 * mm});
            skCircle(sketch, "E90.2.0.0", {"center": v(62.67, 36.43) * mm, "radius": 0.3 * mm});
            skCircle(sketch, "E90.3.0.0", {"center": v(62.67, 37.82) * mm, "radius": 0.3 * mm});
            skCircle(sketch, "E90.4.0.0", {"center": v(62.67, 39.21) * mm, "radius": 0.3 * mm});
            skCircle(sketch, "E90.5.0.0", {"center": v(62.67, 40.6) * mm, "radius": 0.3 * mm});
            skCircle(sketch, "E90.6.0.0", {"center": v(62.67, 42) * mm, "radius": 0.3 * mm});
            skCircle(sketch, "E90.7.0.0", {"center": v(62.67, 43.38) * mm, "radius": 0.3 * mm});
            skCircle(sketch, "E90.8.0.0", {"center": v(62.67, 44.77) * mm, "radius": 0.3 * mm});
            skCircle(sketch, "E90.9.0.0", {"center": v(62.67, 46.16) * mm, "radius": 0.3 * mm});
            skLineSegment(sketch, "E90.direction1", {"start": v(62.67, 33.66) * mm, "end": v(62.67, 35.04) * mm, "construction": true});
            skCircle(sketch, "E91.1.0.0", {"center": v(64.06, 35.04) * mm, "radius": 0.3 * mm});
            skCircle(sketch, "E91.2.0.0", {"center": v(64.06, 36.43) * mm, "radius": 0.3 * mm});
            skCircle(sketch, "E91.3.0.0", {"center": v(64.06, 37.82) * mm, "radius": 0.3 * mm});
            skCircle(sketch, "E91.4.0.0", {"center": v(64.06, 39.21) * mm, "radius": 0.3 * mm});
            skCircle(sketch, "E91.5.0.0", {"center": v(64.06, 40.6) * mm, "radius": 0.3 * mm});
            skCircle(sketch, "E91.6.0.0", {"center": v(64.06, 42) * mm, "radius": 0.3 * mm});
            skCircle(sketch, "E91.7.0.0", {"center": v(64.06, 43.38) * mm, "radius": 0.3 * mm});
            skCircle(sketch, "E91.8.0.0", {"center": v(64.06, 44.77) * mm, "radius": 0.3 * mm});
            skLineSegment(sketch, "E91.direction1", {"start": v(64.06, 33.66) * mm, "end": v(64.06, 35.04) * mm, "construction": true});
            skCircle(sketch, "E92.1.0.0", {"center": v(65.45, 35.04) * mm, "radius": 0.3 * mm});
            skCircle(sketch, "E92.2.0.0", {"center": v(65.45, 36.43) * mm, "radius": 0.3 * mm});
            skCircle(sketch, "E92.3.0.0", {"center": v(65.45, 37.82) * mm, "radius": 0.3 * mm});
            skCircle(sketch, "E92.4.0.0", {"center": v(65.45, 39.21) * mm, "radius": 0.3 * mm});
            skCircle(sketch, "E92.5.0.0", {"center": v(65.45, 40.6) * mm, "radius": 0.3 * mm});
            skCircle(sketch, "E92.6.0.0", {"center": v(65.45, 42) * mm, "radius": 0.3 * mm});
            skCircle(sketch, "E92.7.0.0", {"center": v(65.45, 43.38) * mm, "radius": 0.3 * mm});
            skCircle(sketch, "E92.8.0.0", {"center": v(65.45, 44.77) * mm, "radius": 0.3 * mm});
            skCircle(sketch, "E92.9.0.0", {"center": v(65.45, 46.16) * mm, "radius": 0.3 * mm});
            skLineSegment(sketch, "E92.direction1", {"start": v(65.45, 33.66) * mm, "end": v(65.45, 35.04) * mm, "construction": true});
            skCircle(sketch, "E93.1.0.0", {"center": v(66.84, 35.04) * mm, "radius": 0.3 * mm});
            skCircle(sketch, "E93.2.0.0", {"center": v(66.84, 36.43) * mm, "radius": 0.3 * mm});
            skCircle(sketch, "E93.3.0.0", {"center": v(66.84, 37.82) * mm, "radius": 0.3 * mm});
            skCircle(sketch, "E93.4.0.0", {"center": v(66.84, 39.21) * mm, "radius": 0.3 * mm});
            skCircle(sketch, "E93.5.0.0", {"center": v(66.84, 40.6) * mm, "radius": 0.3 * mm});
            skCircle(sketch, "E93.6.0.0", {"center": v(66.84, 42) * mm, "radius": 0.3 * mm});
            skCircle(sketch, "E93.7.0.0", {"center": v(66.84, 43.38) * mm, "radius": 0.3 * mm});
            skCircle(sketch, "E93.8.0.0", {"center": v(66.84, 44.77) * mm, "radius": 0.3 * mm});
            skLineSegment(sketch, "E93.direction1", {"start": v(66.84, 33.66) * mm, "end": v(66.84, 35.04) * mm, "construction": true});
            skCircle(sketch, "E94.1.0.0", {"center": v(68.23, 35.04) * mm, "radius": 0.3 * mm});
            skCircle(sketch, "E94.2.0.0", {"center": v(68.23, 36.43) * mm, "radius": 0.3 * mm});
            skCircle(sketch, "E94.3.0.0", {"center": v(68.23, 37.82) * mm, "radius": 0.3 * mm});
            skCircle(sketch, "E94.4.0.0", {"center": v(68.23, 39.21) * mm, "radius": 0.3 * mm});
            skCircle(sketch, "E94.5.0.0", {"center": v(68.23, 40.6) * mm, "radius": 0.3 * mm});
            skCircle(sketch, "E94.6.0.0", {"center": v(68.23, 42) * mm, "radius": 0.3 * mm});
            skCircle(sketch, "E94.7.0.0", {"center": v(68.23, 43.38) * mm, "radius": 0.3 * mm});
            skCircle(sketch, "E94.8.0.0", {"center": v(68.23, 44.77) * mm, "radius": 0.3 * mm});
            skCircle(sketch, "E94.9.0.0", {"center": v(68.23, 46.16) * mm, "radius": 0.3 * mm});
            skLineSegment(sketch, "E94.direction1", {"start": v(68.23, 33.66) * mm, "end": v(68.23, 35.04) * mm, "construction": true});
            skCircle(sketch, "E95.1.0.0", {"center": v(69.62, 35.04) * mm, "radius": 0.3 * mm});
            skCircle(sketch, "E95.2.0.0", {"center": v(69.62, 36.43) * mm, "radius": 0.3 * mm});
            skCircle(sketch, "E95.3.0.0", {"center": v(69.62, 37.82) * mm, "radius": 0.3 * mm});
            skCircle(sketch, "E95.4.0.0", {"center": v(69.62, 39.21) * mm, "radius": 0.3 * mm});
            skCircle(sketch, "E95.5.0.0", {"center": v(69.62, 40.6) * mm, "radius": 0.3 * mm});
            skCircle(sketch, "E95.6.0.0", {"center": v(69.62, 42) * mm, "radius": 0.3 * mm});
            skCircle(sketch, "E95.7.0.0", {"center": v(69.62, 43.38) * mm, "radius": 0.3 * mm});
            skCircle(sketch, "E95.8.0.0", {"center": v(69.62, 44.77) * mm, "radius": 0.3 * mm});
            skLineSegment(sketch, "E95.direction1", {"start": v(69.62, 33.66) * mm, "end": v(69.62, 35.04) * mm, "construction": true});
            skCircle(sketch, "E96.1.0.0", {"center": v(71, 35.04) * mm, "radius": 0.3 * mm});
            skCircle(sketch, "E96.2.0.0", {"center": v(71, 36.43) * mm, "radius": 0.3 * mm});
            skCircle(sketch, "E96.3.0.0", {"center": v(71, 37.82) * mm, "radius": 0.3 * mm});
            skCircle(sketch, "E96.4.0.0", {"center": v(71, 39.21) * mm, "radius": 0.3 * mm});
            skCircle(sketch, "E96.5.0.0", {"center": v(71, 40.6) * mm, "radius": 0.3 * mm});
            skCircle(sketch, "E96.6.0.0", {"center": v(71, 42) * mm, "radius": 0.3 * mm});
            skCircle(sketch, "E96.7.0.0", {"center": v(71, 43.38) * mm, "radius": 0.3 * mm});
            skCircle(sketch, "E96.8.0.0", {"center": v(71, 44.77) * mm, "radius": 0.3 * mm});
            skCircle(sketch, "E96.9.0.0", {"center": v(71, 46.16) * mm, "radius": 0.3 * mm});
            skLineSegment(sketch, "E96.direction1", {"start": v(71, 33.66) * mm, "end": v(71, 35.04) * mm, "construction": true});
            skCircle(sketch, "E97.1.0.0", {"center": v(72.4, 35.04) * mm, "radius": 0.3 * mm});
            skCircle(sketch, "E97.2.0.0", {"center": v(72.4, 36.43) * mm, "radius": 0.3 * mm});
            skCircle(sketch, "E97.3.0.0", {"center": v(72.4, 37.82) * mm, "radius": 0.3 * mm});
            skCircle(sketch, "E97.4.0.0", {"center": v(72.4, 39.21) * mm, "radius": 0.3 * mm});
            skCircle(sketch, "E97.5.0.0", {"center": v(72.4, 40.6) * mm, "radius": 0.3 * mm});
            skCircle(sketch, "E97.6.0.0", {"center": v(72.4, 42) * mm, "radius": 0.3 * mm});
            skCircle(sketch, "E97.7.0.0", {"center": v(72.4, 43.38) * mm, "radius": 0.3 * mm});
            skCircle(sketch, "E97.8.0.0", {"center": v(72.4, 44.77) * mm, "radius": 0.3 * mm});
            skLineSegment(sketch, "E97.direction1", {"start": v(72.4, 33.66) * mm, "end": v(72.4, 35.04) * mm, "construction": true});
            skCircle(sketch, "E98.1.0.0", {"center": v(73.79, 35.04) * mm, "radius": 0.3 * mm});
            skCircle(sketch, "E98.2.0.0", {"center": v(73.79, 36.43) * mm, "radius": 0.3 * mm});
            skLineSegment(sketch, "E98.direction1", {"start": v(73.79, 33.66) * mm, "end": v(73.79, 35.04) * mm, "construction": true});
            skCircle(sketch, "E99.0.3.0", {"center": v(73.79, 37.82) * mm, "radius": 0.3 * mm});
            skCircle(sketch, "E99.0.4.0", {"center": v(73.79, 39.21) * mm, "radius": 0.3 * mm});
            skCircle(sketch, "E99.0.5.0", {"center": v(73.79, 40.6) * mm, "radius": 0.3 * mm});
            skCircle(sketch, "E99.0.6.0", {"center": v(73.79, 42) * mm, "radius": 0.3 * mm});
            skCircle(sketch, "E99.0.7.0", {"center": v(73.79, 43.38) * mm, "radius": 0.3 * mm});
            skCircle(sketch, "E99.0.8.0", {"center": v(73.79, 44.77) * mm, "radius": 0.3 * mm});
            skCircle(sketch, "E99.0.9.0", {"center": v(73.79, 46.16) * mm, "radius": 0.3 * mm});
            skCircle(sketch, "E100.1.0.0", {"center": v(75.18, 35.04) * mm, "radius": 0.3 * mm});
            skCircle(sketch, "E100.2.0.0", {"center": v(75.18, 36.43) * mm, "radius": 0.3 * mm});
            skCircle(sketch, "E100.3.0.0", {"center": v(75.18, 37.82) * mm, "radius": 0.3 * mm});
            skCircle(sketch, "E100.4.0.0", {"center": v(75.18, 39.21) * mm, "radius": 0.3 * mm});
            skCircle(sketch, "E100.5.0.0", {"center": v(75.18, 40.6) * mm, "radius": 0.3 * mm});
            skCircle(sketch, "E100.6.0.0", {"center": v(75.18, 42) * mm, "radius": 0.3 * mm});
            skCircle(sketch, "E100.7.0.0", {"center": v(75.18, 43.38) * mm, "radius": 0.3 * mm});
            skCircle(sketch, "E100.8.0.0", {"center": v(75.18, 44.77) * mm, "radius": 0.3 * mm});
            skLineSegment(sketch, "E100.direction1", {"start": v(75.18, 33.66) * mm, "end": v(75.18, 35.04) * mm, "construction": true});
            skCircle(sketch, "E101.1.0.0", {"center": v(62.67, 57.66) * mm, "radius": 0.3 * mm});
            skCircle(sketch, "E101.2.0.0", {"center": v(62.67, 56.27) * mm, "radius": 0.3 * mm});
            skCircle(sketch, "E101.3.0.0", {"center": v(62.67, 54.88) * mm, "radius": 0.3 * mm});
            skCircle(sketch, "E101.4.0.0", {"center": v(62.67, 53.5) * mm, "radius": 0.3 * mm});
            skCircle(sketch, "E101.5.0.0", {"center": v(62.67, 52.1) * mm, "radius": 0.3 * mm});
            skCircle(sketch, "E101.6.0.0", {"center": v(62.67, 50.72) * mm, "radius": 0.3 * mm});
            skCircle(sketch, "E101.7.0.0", {"center": v(62.67, 49.33) * mm, "radius": 0.3 * mm});
            skCircle(sketch, "E101.8.0.0", {"center": v(62.67, 47.94) * mm, "radius": 0.3 * mm});
            skLineSegment(sketch, "E101.direction1", {"start": v(62.67, 59.05) * mm, "end": v(62.67, 57.66) * mm, "construction": true});
            skCircle(sketch, "E102.1.0.0", {"center": v(64.06, 57.66) * mm, "radius": 0.3 * mm});
            skCircle(sketch, "E102.2.0.0", {"center": v(64.06, 56.27) * mm, "radius": 0.3 * mm});
            skCircle(sketch, "E102.3.0.0", {"center": v(64.06, 54.88) * mm, "radius": 0.3 * mm});
            skCircle(sketch, "E102.4.0.0", {"center": v(64.06, 53.5) * mm, "radius": 0.3 * mm});
            skCircle(sketch, "E102.5.0.0", {"center": v(64.06, 52.1) * mm, "radius": 0.3 * mm});
            skCircle(sketch, "E102.6.0.0", {"center": v(64.06, 50.72) * mm, "radius": 0.3 * mm});
            skCircle(sketch, "E102.7.0.0", {"center": v(64.06, 49.33) * mm, "radius": 0.3 * mm});
            skCircle(sketch, "E102.8.0.0", {"center": v(64.06, 47.94) * mm, "radius": 0.3 * mm});
            skCircle(sketch, "E102.9.0.0", {"center": v(64.06, 46.55) * mm, "radius": 0.3 * mm});
            skLineSegment(sketch, "E102.direction1", {"start": v(64.06, 59.05) * mm, "end": v(64.06, 57.66) * mm, "construction": true});
            skCircle(sketch, "E103.1.0.0", {"center": v(65.45, 57.66) * mm, "radius": 0.3 * mm});
            skCircle(sketch, "E103.2.0.0", {"center": v(65.45, 56.27) * mm, "radius": 0.3 * mm});
            skCircle(sketch, "E103.3.0.0", {"center": v(65.45, 54.88) * mm, "radius": 0.3 * mm});
            skCircle(sketch, "E103.4.0.0", {"center": v(65.45, 53.5) * mm, "radius": 0.3 * mm});
            skCircle(sketch, "E103.5.0.0", {"center": v(65.45, 52.1) * mm, "radius": 0.3 * mm});
            skCircle(sketch, "E103.6.0.0", {"center": v(65.45, 50.72) * mm, "radius": 0.3 * mm});
            skCircle(sketch, "E103.7.0.0", {"center": v(65.45, 49.33) * mm, "radius": 0.3 * mm});
            skCircle(sketch, "E103.8.0.0", {"center": v(65.45, 47.94) * mm, "radius": 0.3 * mm});
            skLineSegment(sketch, "E103.direction1", {"start": v(65.45, 59.05) * mm, "end": v(65.45, 57.66) * mm, "construction": true});
            skCircle(sketch, "E104.1.0.0", {"center": v(66.84, 57.66) * mm, "radius": 0.3 * mm});
            skCircle(sketch, "E104.2.0.0", {"center": v(66.84, 56.27) * mm, "radius": 0.3 * mm});
            skCircle(sketch, "E104.3.0.0", {"center": v(66.84, 54.88) * mm, "radius": 0.3 * mm});
            skCircle(sketch, "E104.4.0.0", {"center": v(66.84, 53.5) * mm, "radius": 0.3 * mm});
            skCircle(sketch, "E104.5.0.0", {"center": v(66.84, 52.1) * mm, "radius": 0.3 * mm});
            skCircle(sketch, "E104.6.0.0", {"center": v(66.84, 50.72) * mm, "radius": 0.3 * mm});
            skCircle(sketch, "E104.7.0.0", {"center": v(66.84, 49.33) * mm, "radius": 0.3 * mm});
            skCircle(sketch, "E104.8.0.0", {"center": v(66.84, 47.94) * mm, "radius": 0.3 * mm});
            skCircle(sketch, "E104.9.0.0", {"center": v(66.84, 46.55) * mm, "radius": 0.3 * mm});
            skLineSegment(sketch, "E104.direction1", {"start": v(66.84, 59.05) * mm, "end": v(66.84, 57.66) * mm, "construction": true});
            skCircle(sketch, "E105.1.0.0", {"center": v(68.23, 57.66) * mm, "radius": 0.3 * mm});
            skCircle(sketch, "E105.2.0.0", {"center": v(68.23, 56.27) * mm, "radius": 0.3 * mm});
            skCircle(sketch, "E105.3.0.0", {"center": v(68.23, 54.88) * mm, "radius": 0.3 * mm});
            skCircle(sketch, "E105.4.0.0", {"center": v(68.23, 53.5) * mm, "radius": 0.3 * mm});
            skCircle(sketch, "E105.5.0.0", {"center": v(68.23, 52.1) * mm, "radius": 0.3 * mm});
            skCircle(sketch, "E105.6.0.0", {"center": v(68.23, 50.72) * mm, "radius": 0.3 * mm});
            skCircle(sketch, "E105.7.0.0", {"center": v(68.23, 49.33) * mm, "radius": 0.3 * mm});
            skCircle(sketch, "E105.8.0.0", {"center": v(68.23, 47.94) * mm, "radius": 0.3 * mm});
            skLineSegment(sketch, "E105.direction1", {"start": v(68.23, 59.05) * mm, "end": v(68.23, 57.66) * mm, "construction": true});
            skCircle(sketch, "E106.1.0.0", {"center": v(69.62, 57.66) * mm, "radius": 0.3 * mm});
            skCircle(sketch, "E106.2.0.0", {"center": v(69.62, 56.27) * mm, "radius": 0.3 * mm});
            skCircle(sketch, "E106.3.0.0", {"center": v(69.62, 54.88) * mm, "radius": 0.3 * mm});
            skCircle(sketch, "E106.4.0.0", {"center": v(69.62, 53.5) * mm, "radius": 0.3 * mm});
            skCircle(sketch, "E106.5.0.0", {"center": v(69.62, 52.1) * mm, "radius": 0.3 * mm});
            skCircle(sketch, "E106.6.0.0", {"center": v(69.62, 50.72) * mm, "radius": 0.3 * mm});
            skCircle(sketch, "E106.7.0.0", {"center": v(69.62, 49.33) * mm, "radius": 0.3 * mm});
            skCircle(sketch, "E106.8.0.0", {"center": v(69.62, 47.94) * mm, "radius": 0.3 * mm});
            skCircle(sketch, "E106.9.0.0", {"center": v(69.62, 46.55) * mm, "radius": 0.3 * mm});
            skLineSegment(sketch, "E106.direction1", {"start": v(69.62, 59.05) * mm, "end": v(69.62, 57.66) * mm, "construction": true});
            skCircle(sketch, "E107.1.0.0", {"center": v(71, 57.66) * mm, "radius": 0.3 * mm});
            skCircle(sketch, "E107.2.0.0", {"center": v(71, 56.27) * mm, "radius": 0.3 * mm});
            skCircle(sketch, "E107.3.0.0", {"center": v(71, 54.88) * mm, "radius": 0.3 * mm});
            skCircle(sketch, "E107.4.0.0", {"center": v(71, 53.5) * mm, "radius": 0.3 * mm});
            skCircle(sketch, "E107.5.0.0", {"center": v(71, 52.1) * mm, "radius": 0.3 * mm});
            skCircle(sketch, "E107.6.0.0", {"center": v(71, 50.72) * mm, "radius": 0.3 * mm});
            skCircle(sketch, "E107.7.0.0", {"center": v(71, 49.33) * mm, "radius": 0.3 * mm});
            skCircle(sketch, "E107.8.0.0", {"center": v(71, 47.94) * mm, "radius": 0.3 * mm});
            skLineSegment(sketch, "E107.direction1", {"start": v(71, 59.05) * mm, "end": v(71, 57.66) * mm, "construction": true});
            skCircle(sketch, "E108.1.0.0", {"center": v(72.4, 57.66) * mm, "radius": 0.3 * mm});
            skCircle(sketch, "E108.2.0.0", {"center": v(72.4, 56.27) * mm, "radius": 0.3 * mm});
            skCircle(sketch, "E108.3.0.0", {"center": v(72.4, 54.88) * mm, "radius": 0.3 * mm});
            skCircle(sketch, "E108.4.0.0", {"center": v(72.4, 53.5) * mm, "radius": 0.3 * mm});
            skCircle(sketch, "E108.5.0.0", {"center": v(72.4, 52.1) * mm, "radius": 0.3 * mm});
            skCircle(sketch, "E108.6.0.0", {"center": v(72.4, 50.72) * mm, "radius": 0.3 * mm});
            skCircle(sketch, "E108.7.0.0", {"center": v(72.4, 49.33) * mm, "radius": 0.3 * mm});
            skCircle(sketch, "E108.8.0.0", {"center": v(72.4, 47.94) * mm, "radius": 0.3 * mm});
            skCircle(sketch, "E108.9.0.0", {"center": v(72.4, 46.55) * mm, "radius": 0.3 * mm});
            skLineSegment(sketch, "E108.direction1", {"start": v(72.4, 59.05) * mm, "end": v(72.4, 57.66) * mm, "construction": true});
            skCircle(sketch, "E109.1.0.0", {"center": v(73.79, 57.66) * mm, "radius": 0.3 * mm});
            skCircle(sketch, "E109.2.0.0", {"center": v(73.79, 56.27) * mm, "radius": 0.3 * mm});
            skCircle(sketch, "E109.3.0.0", {"center": v(73.79, 54.88) * mm, "radius": 0.3 * mm});
            skCircle(sketch, "E109.4.0.0", {"center": v(73.79, 53.5) * mm, "radius": 0.3 * mm});
            skCircle(sketch, "E109.5.0.0", {"center": v(73.79, 52.1) * mm, "radius": 0.3 * mm});
            skCircle(sketch, "E109.6.0.0", {"center": v(73.79, 50.72) * mm, "radius": 0.3 * mm});
            skCircle(sketch, "E109.7.0.0", {"center": v(73.79, 49.33) * mm, "radius": 0.3 * mm});
            skCircle(sketch, "E109.8.0.0", {"center": v(73.79, 47.94) * mm, "radius": 0.3 * mm});
            skLineSegment(sketch, "E109.direction1", {"start": v(73.79, 59.05) * mm, "end": v(73.79, 57.66) * mm, "construction": true});
            skCircle(sketch, "E110.1.0.0", {"center": v(75.18, 57.66) * mm, "radius": 0.3 * mm});
            skCircle(sketch, "E110.2.0.0", {"center": v(75.18, 56.27) * mm, "radius": 0.3 * mm});
            skCircle(sketch, "E110.3.0.0", {"center": v(75.18, 54.88) * mm, "radius": 0.3 * mm});
            skCircle(sketch, "E110.4.0.0", {"center": v(75.18, 53.5) * mm, "radius": 0.3 * mm});
            skCircle(sketch, "E110.5.0.0", {"center": v(75.18, 52.1) * mm, "radius": 0.3 * mm});
            skCircle(sketch, "E110.6.0.0", {"center": v(75.18, 50.72) * mm, "radius": 0.3 * mm});
            skCircle(sketch, "E110.7.0.0", {"center": v(75.18, 49.33) * mm, "radius": 0.3 * mm});
            skCircle(sketch, "E110.8.0.0", {"center": v(75.18, 47.94) * mm, "radius": 0.3 * mm});
            skCircle(sketch, "E110.9.0.0", {"center": v(75.18, 46.55) * mm, "radius": 0.3 * mm});
            skLineSegment(sketch, "E110.direction1", {"start": v(75.18, 59.05) * mm, "end": v(75.18, 57.66) * mm, "construction": true});
            skCircle(sketch, "E111.1.0.0", {"center": v(76.56, 57.66) * mm, "radius": 0.3 * mm});
            skCircle(sketch, "E111.2.0.0", {"center": v(76.56, 56.27) * mm, "radius": 0.3 * mm});
            skCircle(sketch, "E111.3.0.0", {"center": v(76.56, 54.88) * mm, "radius": 0.3 * mm});
            skCircle(sketch, "E111.4.0.0", {"center": v(76.56, 53.5) * mm, "radius": 0.3 * mm});
            skCircle(sketch, "E111.5.0.0", {"center": v(76.56, 52.1) * mm, "radius": 0.3 * mm});
            skCircle(sketch, "E111.6.0.0", {"center": v(76.56, 50.72) * mm, "radius": 0.3 * mm});
            skCircle(sketch, "E111.7.0.0", {"center": v(76.56, 49.33) * mm, "radius": 0.3 * mm});
            skCircle(sketch, "E111.8.0.0", {"center": v(76.56, 47.94) * mm, "radius": 0.3 * mm});
            skLineSegment(sketch, "E111.direction1", {"start": v(76.56, 59.05) * mm, "end": v(76.56, 57.66) * mm, "construction": true});
            skCircle(sketch, "E112.1.0.0", {"center": v(76.56, 35.04) * mm, "radius": 0.3 * mm});
            skCircle(sketch, "E112.2.0.0", {"center": v(76.56, 36.43) * mm, "radius": 0.3 * mm});
            skCircle(sketch, "E112.3.0.0", {"center": v(76.56, 37.82) * mm, "radius": 0.3 * mm});
            skCircle(sketch, "E112.4.0.0", {"center": v(76.56, 39.21) * mm, "radius": 0.3 * mm});
            skCircle(sketch, "E112.5.0.0", {"center": v(76.56, 40.6) * mm, "radius": 0.3 * mm});
            skCircle(sketch, "E112.6.0.0", {"center": v(76.56, 42) * mm, "radius": 0.3 * mm});
            skCircle(sketch, "E112.7.0.0", {"center": v(76.56, 43.38) * mm, "radius": 0.3 * mm});
            skCircle(sketch, "E112.8.0.0", {"center": v(76.56, 44.77) * mm, "radius": 0.3 * mm});
            skCircle(sketch, "E112.9.0.0", {"center": v(76.56, 46.16) * mm, "radius": 0.3 * mm});
            skLineSegment(sketch, "E112.direction1", {"start": v(76.56, 33.66) * mm, "end": v(76.56, 35.04) * mm, "construction": true});
            skCircle(sketch, "E113.0.9.0", {"center": v(59.9, 46.55) * mm, "radius": 0.3 * mm});
            skCircle(sketch, "E114.0.9.0", {"center": v(62.67, 46.55) * mm, "radius": 0.3 * mm});
            skCircle(sketch, "E115.0.9.0", {"center": v(65.45, 46.55) * mm, "radius": 0.3 * mm});
            skCircle(sketch, "E116.0.9.0", {"center": v(68.23, 46.55) * mm, "radius": 0.3 * mm});
            skCircle(sketch, "E117.0.9.0", {"center": v(71, 46.55) * mm, "radius": 0.3 * mm});
            skCircle(sketch, "E118.0.9.0", {"center": v(73.79, 46.55) * mm, "radius": 0.3 * mm});
            skCircle(sketch, "E119.0.9.0", {"center": v(76.56, 46.55) * mm, "radius": 0.3 * mm});
            skCircle(sketch, "E120.0.9.0", {"center": v(61.29, 46.16) * mm, "radius": 0.3 * mm});
            skCircle(sketch, "E121.0.9.0", {"center": v(66.84, 46.16) * mm, "radius": 0.3 * mm});
            skCircle(sketch, "E122.0.9.0", {"center": v(72.4, 46.16) * mm, "radius": 0.3 * mm});
            skCircle(sketch, "E123.0.9.0", {"center": v(75.18, 46.16) * mm, "radius": 0.3 * mm});
            skCircle(sketch, "E124.0.9.0", {"center": v(64.06, 46.16) * mm, "radius": 0.3 * mm});
            skCircle(sketch, "E125.0.9.0", {"center": v(69.62, 46.16) * mm, "radius": 0.3 * mm});
            skSolve(sketch);
        }
        {
            var Q0;
            Q0 = qSketchRegion(id + "F16", true);
            var Q1;
            {var subQ0=sQuery(id+"F11.wireOp",EDGE,"E76");Q1=makeQuery(id+"F12.boolean.opBoolean","SPLIT",FACE,{"disambiguationData":[TD([makeQuery(id+"F9.opExtrude","SWEPT_FACE",FACE,{"disambiguationData":[OSD([sQuery(id+"F8.wireOp",EDGE,"E74")])]})])],"derivedFrom":makeQuery(id+"F12.opExtrude","SWEPT_FACE",FACE,{"disambiguationData":[OSD([subQ0])]})});}
            extrude(context, id + "F17", {"entities" : qUnion([Q0]), "operationType" : NewBodyOperationType.ADD, "endBoundEntityFace" : qUnion([Q1]), "depth" : 17.78 * mm + 9.52 * mm});
        }
        {
            var Q0;
            Q0=qCreatedBy(makeId("Top.planeOp"),FACE);
            var sketch = newSketch(context, id + "F18", { "sketchPlane" : qUnion([Q0])});
            skCircle(sketch, "E126", {"center": v(77.96, 33.66) * mm, "radius": 0.3 * mm});
            skCircle(sketch, "E127", {"center": v(79.35, 33.66) * mm, "radius": 0.3 * mm});
            skCircle(sketch, "E128", {"center": v(80.74, 33.66) * mm, "radius": 0.3 * mm});
            skCircle(sketch, "E129", {"center": v(82.13, 33.66) * mm, "radius": 0.3 * mm});
            skCircle(sketch, "E130", {"center": v(83.52, 33.66) * mm, "radius": 0.3 * mm});
            skCircle(sketch, "E131.1.0.0", {"center": v(77.96, 35.04) * mm, "radius": 0.3 * mm});
            skCircle(sketch, "E131.2.0.0", {"center": v(77.96, 36.43) * mm, "radius": 0.3 * mm});
            skCircle(sketch, "E131.3.0.0", {"center": v(77.96, 37.82) * mm, "radius": 0.3 * mm});
            skCircle(sketch, "E131.4.0.0", {"center": v(77.96, 39.21) * mm, "radius": 0.3 * mm});
            skCircle(sketch, "E131.5.0.0", {"center": v(77.96, 40.6) * mm, "radius": 0.3 * mm});
            skCircle(sketch, "E131.6.0.0", {"center": v(77.96, 41.99) * mm, "radius": 0.3 * mm});
            skCircle(sketch, "E131.7.0.0", {"center": v(77.96, 43.38) * mm, "radius": 0.3 * mm});
            skCircle(sketch, "E131.8.0.0", {"center": v(77.96, 44.77) * mm, "radius": 0.3 * mm});
            skCircle(sketch, "E131.9.0.0", {"center": v(77.96, 46.16) * mm, "radius": 0.3 * mm});
            skLineSegment(sketch, "E131.direction1", {"start": v(77.96, 33.66) * mm, "end": v(77.96, 35.04) * mm, "construction": true});
            skLineSegment(sketch, "E132", {"start": v(76.96, 46.36) * mm, "end": v(80.7, 46.36) * mm});
            skCircle(sketch, "E133.MirrorC", {"center": v(77.96, 59.05) * mm, "radius": 0.3 * mm});
            skCircle(sketch, "E134.MirrorC", {"center": v(79.35, 59.05) * mm, "radius": 0.3 * mm});
            skCircle(sketch, "E135.MirrorC", {"center": v(80.74, 59.05) * mm, "radius": 0.3 * mm});
            skCircle(sketch, "E136.MirrorC", {"center": v(82.13, 59.05) * mm, "radius": 0.3 * mm});
            skCircle(sketch, "E137.MirrorC", {"center": v(83.52, 59.05) * mm, "radius": 0.3 * mm});
            skCircle(sketch, "E138.1.0.0", {"center": v(79.35, 35.04) * mm, "radius": 0.3 * mm});
            skCircle(sketch, "E138.2.0.0", {"center": v(79.35, 36.43) * mm, "radius": 0.3 * mm});
            skCircle(sketch, "E138.3.0.0", {"center": v(79.35, 37.82) * mm, "radius": 0.3 * mm});
            skCircle(sketch, "E138.4.0.0", {"center": v(79.35, 39.21) * mm, "radius": 0.3 * mm});
            skCircle(sketch, "E138.5.0.0", {"center": v(79.35, 40.6) * mm, "radius": 0.3 * mm});
            skCircle(sketch, "E138.6.0.0", {"center": v(79.35, 41.99) * mm, "radius": 0.3 * mm});
            skCircle(sketch, "E138.7.0.0", {"center": v(79.35, 43.38) * mm, "radius": 0.3 * mm});
            skCircle(sketch, "E138.8.0.0", {"center": v(79.35, 44.77) * mm, "radius": 0.3 * mm});
            skLineSegment(sketch, "E138.direction1", {"start": v(79.35, 33.66) * mm, "end": v(79.35, 35.04) * mm, "construction": true});
            skCircle(sketch, "E139.1.0.0", {"center": v(80.74, 35.04) * mm, "radius": 0.3 * mm});
            skCircle(sketch, "E139.2.0.0", {"center": v(80.74, 36.43) * mm, "radius": 0.3 * mm});
            skCircle(sketch, "E139.3.0.0", {"center": v(80.74, 37.82) * mm, "radius": 0.3 * mm});
            skCircle(sketch, "E139.4.0.0", {"center": v(80.74, 39.21) * mm, "radius": 0.3 * mm});
            skCircle(sketch, "E139.5.0.0", {"center": v(80.74, 40.6) * mm, "radius": 0.3 * mm});
            skCircle(sketch, "E139.6.0.0", {"center": v(80.74, 41.99) * mm, "radius": 0.3 * mm});
            skCircle(sketch, "E139.7.0.0", {"center": v(80.74, 43.38) * mm, "radius": 0.3 * mm});
            skCircle(sketch, "E139.8.0.0", {"center": v(80.74, 44.77) * mm, "radius": 0.3 * mm});
            skCircle(sketch, "E139.9.0.0", {"center": v(80.74, 46.16) * mm, "radius": 0.3 * mm});
            skLineSegment(sketch, "E139.direction1", {"start": v(80.74, 33.66) * mm, "end": v(80.74, 35.04) * mm, "construction": true});
            skCircle(sketch, "E140.1.0.0", {"center": v(82.13, 35.04) * mm, "radius": 0.3 * mm});
            skCircle(sketch, "E140.2.0.0", {"center": v(82.13, 36.43) * mm, "radius": 0.3 * mm});
            skCircle(sketch, "E140.3.0.0", {"center": v(82.13, 37.82) * mm, "radius": 0.3 * mm});
            skCircle(sketch, "E140.4.0.0", {"center": v(82.13, 39.21) * mm, "radius": 0.3 * mm});
            skCircle(sketch, "E140.5.0.0", {"center": v(82.13, 40.6) * mm, "radius": 0.3 * mm});
            skCircle(sketch, "E140.6.0.0", {"center": v(82.13, 41.99) * mm, "radius": 0.3 * mm});
            skCircle(sketch, "E140.7.0.0", {"center": v(82.13, 43.38) * mm, "radius": 0.3 * mm});
            skCircle(sketch, "E140.8.0.0", {"center": v(82.13, 44.77) * mm, "radius": 0.3 * mm});
            skLineSegment(sketch, "E140.direction1", {"start": v(82.13, 33.66) * mm, "end": v(82.13, 35.04) * mm, "construction": true});
            skCircle(sketch, "E141.1.0.0", {"center": v(83.52, 35.04) * mm, "radius": 0.3 * mm});
            skCircle(sketch, "E141.2.0.0", {"center": v(83.52, 36.43) * mm, "radius": 0.3 * mm});
            skLineSegment(sketch, "E141.direction1", {"start": v(83.52, 33.66) * mm, "end": v(83.52, 35.04) * mm, "construction": true});
            skCircle(sketch, "E142.0.3.0", {"center": v(83.52, 37.82) * mm, "radius": 0.3 * mm});
            skCircle(sketch, "E142.0.4.0", {"center": v(83.52, 39.21) * mm, "radius": 0.3 * mm});
            skCircle(sketch, "E142.0.5.0", {"center": v(83.52, 40.6) * mm, "radius": 0.3 * mm});
            skCircle(sketch, "E142.0.6.0", {"center": v(83.52, 41.99) * mm, "radius": 0.3 * mm});
            skCircle(sketch, "E142.0.7.0", {"center": v(83.52, 43.38) * mm, "radius": 0.3 * mm});
            skCircle(sketch, "E142.0.8.0", {"center": v(83.52, 44.77) * mm, "radius": 0.3 * mm});
            skCircle(sketch, "E142.0.9.0", {"center": v(83.52, 46.16) * mm, "radius": 0.3 * mm});
            skCircle(sketch, "E143.1.0.0", {"center": v(77.96, 57.67) * mm, "radius": 0.3 * mm});
            skCircle(sketch, "E143.2.0.0", {"center": v(77.96, 56.28) * mm, "radius": 0.3 * mm});
            skCircle(sketch, "E143.3.0.0", {"center": v(77.96, 54.89) * mm, "radius": 0.3 * mm});
            skCircle(sketch, "E143.4.0.0", {"center": v(77.96, 53.5) * mm, "radius": 0.3 * mm});
            skCircle(sketch, "E143.5.0.0", {"center": v(77.96, 52.1) * mm, "radius": 0.3 * mm});
            skCircle(sketch, "E143.6.0.0", {"center": v(77.96, 50.72) * mm, "radius": 0.3 * mm});
            skCircle(sketch, "E143.7.0.0", {"center": v(77.96, 49.33) * mm, "radius": 0.3 * mm});
            skCircle(sketch, "E143.8.0.0", {"center": v(77.96, 47.94) * mm, "radius": 0.3 * mm});
            skLineSegment(sketch, "E143.direction1", {"start": v(77.96, 59.05) * mm, "end": v(77.96, 57.67) * mm, "construction": true});
            skCircle(sketch, "E144.0.9.0", {"center": v(77.96, 46.55) * mm, "radius": 0.3 * mm});
            skCircle(sketch, "E145.0.9.0", {"center": v(82.13, 46.16) * mm, "radius": 0.3 * mm});
            skCircle(sketch, "E146.0.9.0", {"center": v(79.35, 46.16) * mm, "radius": 0.3 * mm});
            skLineSegment(sketch, "E147.MirrorCS", {"start": v(82.13, 59.05) * mm, "end": v(82.13, 57.67) * mm, "construction": true});
            skLineSegment(sketch, "E148.MirrorCS", {"start": v(80.74, 59.05) * mm, "end": v(80.74, 57.67) * mm, "construction": true});
            skCircle(sketch, "E149.MirrorC", {"center": v(80.74, 46.55) * mm, "radius": 0.3 * mm});
            skCircle(sketch, "E150.MirrorC", {"center": v(80.74, 57.67) * mm, "radius": 0.3 * mm});
            skCircle(sketch, "E151.MirrorC", {"center": v(79.35, 57.67) * mm, "radius": 0.3 * mm});
            skCircle(sketch, "E152.MirrorC", {"center": v(83.52, 57.67) * mm, "radius": 0.3 * mm});
            skCircle(sketch, "E153.MirrorC", {"center": v(82.13, 57.67) * mm, "radius": 0.3 * mm});
            skLineSegment(sketch, "E154.MirrorCS", {"start": v(83.52, 59.05) * mm, "end": v(83.52, 57.67) * mm, "construction": true});
            skLineSegment(sketch, "E155.MirrorCS", {"start": v(79.35, 59.05) * mm, "end": v(79.35, 57.67) * mm, "construction": true});
            skCircle(sketch, "E156.MirrorC", {"center": v(80.74, 54.89) * mm, "radius": 0.3 * mm});
            skCircle(sketch, "E157.MirrorC", {"center": v(79.35, 54.89) * mm, "radius": 0.3 * mm});
            skCircle(sketch, "E158.MirrorC", {"center": v(83.52, 50.72) * mm, "radius": 0.3 * mm});
            skCircle(sketch, "E159.MirrorC", {"center": v(82.13, 52.1) * mm, "radius": 0.3 * mm});
            skCircle(sketch, "E160.MirrorC", {"center": v(79.35, 47.94) * mm, "radius": 0.3 * mm});
            skCircle(sketch, "E161.MirrorC", {"center": v(79.35, 56.28) * mm, "radius": 0.3 * mm});
            skCircle(sketch, "E162.MirrorC", {"center": v(79.35, 46.55) * mm, "radius": 0.3 * mm});
            skCircle(sketch, "E163.MirrorC", {"center": v(82.13, 47.94) * mm, "radius": 0.3 * mm});
            skCircle(sketch, "E164.MirrorC", {"center": v(83.52, 52.1) * mm, "radius": 0.3 * mm});
            skCircle(sketch, "E165.MirrorC", {"center": v(80.74, 56.28) * mm, "radius": 0.3 * mm});
            skCircle(sketch, "E166.MirrorC", {"center": v(80.74, 47.94) * mm, "radius": 0.3 * mm});
            skCircle(sketch, "E167.MirrorC", {"center": v(83.52, 53.5) * mm, "radius": 0.3 * mm});
            skCircle(sketch, "E168.MirrorC", {"center": v(82.13, 49.33) * mm, "radius": 0.3 * mm});
            skCircle(sketch, "E169.MirrorC", {"center": v(82.13, 46.55) * mm, "radius": 0.3 * mm});
            skCircle(sketch, "E170.MirrorC", {"center": v(82.13, 56.28) * mm, "radius": 0.3 * mm});
            skCircle(sketch, "E171.MirrorC", {"center": v(79.35, 52.1) * mm, "radius": 0.3 * mm});
            skCircle(sketch, "E172.MirrorC", {"center": v(83.52, 47.94) * mm, "radius": 0.3 * mm});
            skCircle(sketch, "E173.MirrorC", {"center": v(79.35, 49.33) * mm, "radius": 0.3 * mm});
            skCircle(sketch, "E174.MirrorC", {"center": v(82.13, 53.5) * mm, "radius": 0.3 * mm});
            skCircle(sketch, "E175.MirrorC", {"center": v(83.52, 49.33) * mm, "radius": 0.3 * mm});
            skCircle(sketch, "E176.MirrorC", {"center": v(80.74, 53.5) * mm, "radius": 0.3 * mm});
            skCircle(sketch, "E177.MirrorC", {"center": v(83.52, 56.28) * mm, "radius": 0.3 * mm});
            skCircle(sketch, "E178.MirrorC", {"center": v(80.74, 52.1) * mm, "radius": 0.3 * mm});
            skCircle(sketch, "E179.MirrorC", {"center": v(83.52, 46.55) * mm, "radius": 0.3 * mm});
            skCircle(sketch, "E180.MirrorC", {"center": v(82.13, 54.89) * mm, "radius": 0.3 * mm});
            skCircle(sketch, "E181.MirrorC", {"center": v(79.35, 53.5) * mm, "radius": 0.3 * mm});
            skCircle(sketch, "E182.MirrorC", {"center": v(80.74, 50.72) * mm, "radius": 0.3 * mm});
            skCircle(sketch, "E183.MirrorC", {"center": v(80.74, 49.33) * mm, "radius": 0.3 * mm});
            skCircle(sketch, "E184.MirrorC", {"center": v(83.52, 54.89) * mm, "radius": 0.3 * mm});
            skCircle(sketch, "E185.MirrorC", {"center": v(82.13, 50.72) * mm, "radius": 0.3 * mm});
            skCircle(sketch, "E186.MirrorC", {"center": v(79.35, 50.72) * mm, "radius": 0.3 * mm});
            skSolve(sketch);
        }
        {
            var Q0;
            Q0 = qSketchRegion(id + "F18", true);
            var Q1;
            Q1=makeQuery(id+"F17.opExtrude","CAP_FACE",FACE,{"disambiguationData":[OSD([sQuery(id+"F16.wireOp",EDGE,"E81.15.0.0")])],"isStart":false});
            extrude(context, id + "F19", {"entities" : qUnion([Q0]), "operationType" : NewBodyOperationType.ADD, "endBound" : BoundingType.UP_TO_SURFACE, "endBoundEntityFace" : qUnion([Q1]), "depth" : 25 * mm});
        }
        {
            var Q0;
            Q0=makeQuery(id+"F3.boolean.opBoolean","COPY",FACE,{"derivedFrom":makeQuery(id+"F3.opExtrude","SWEPT_FACE",FACE,{"disambiguationData":[OSD([sQuery(id+"F2.wireOp",EDGE,"E20")])]})});
            var sketch = newSketch(context, id + "F20", { "sketchPlane" : qUnion([Q0])});
            skCircle(sketch, "E187", {"center": v(37.21, 5.46) * mm, "radius": 4.69 * mm});
            skSolve(sketch);
        }
        {
            var Q0;
            Q0=makeQuery(id+"F20.imprint","IMPRINT",FACE,{"disambiguationData":[TD([[makeQuery(id+"F20.imprint","IMPRINT",EDGE,{"derivedFrom":sQuery(id+"F20.wireOp",EDGE,"E187")}),1.0]])]});
            extrude(context, id + "F21", {"entities" : qUnion([Q0]), "operationType" : NewBodyOperationType.REMOVE, "oppositeDirection" : true, "depth" : 0.1 * mm});
        }
        {
            var Q0;
            Q0=qCreatedBy(makeId("Front.planeOp"),FACE);
            cPlane(context, id + "F22", {"entities" : qUnion([Q0]), "cplaneType" : CPlaneType.OFFSET, "offset" : 46.35 * mm, "oppositeDirection" : true, "width" : 150 * mm, "height" : 150 * mm});
        }
    });
